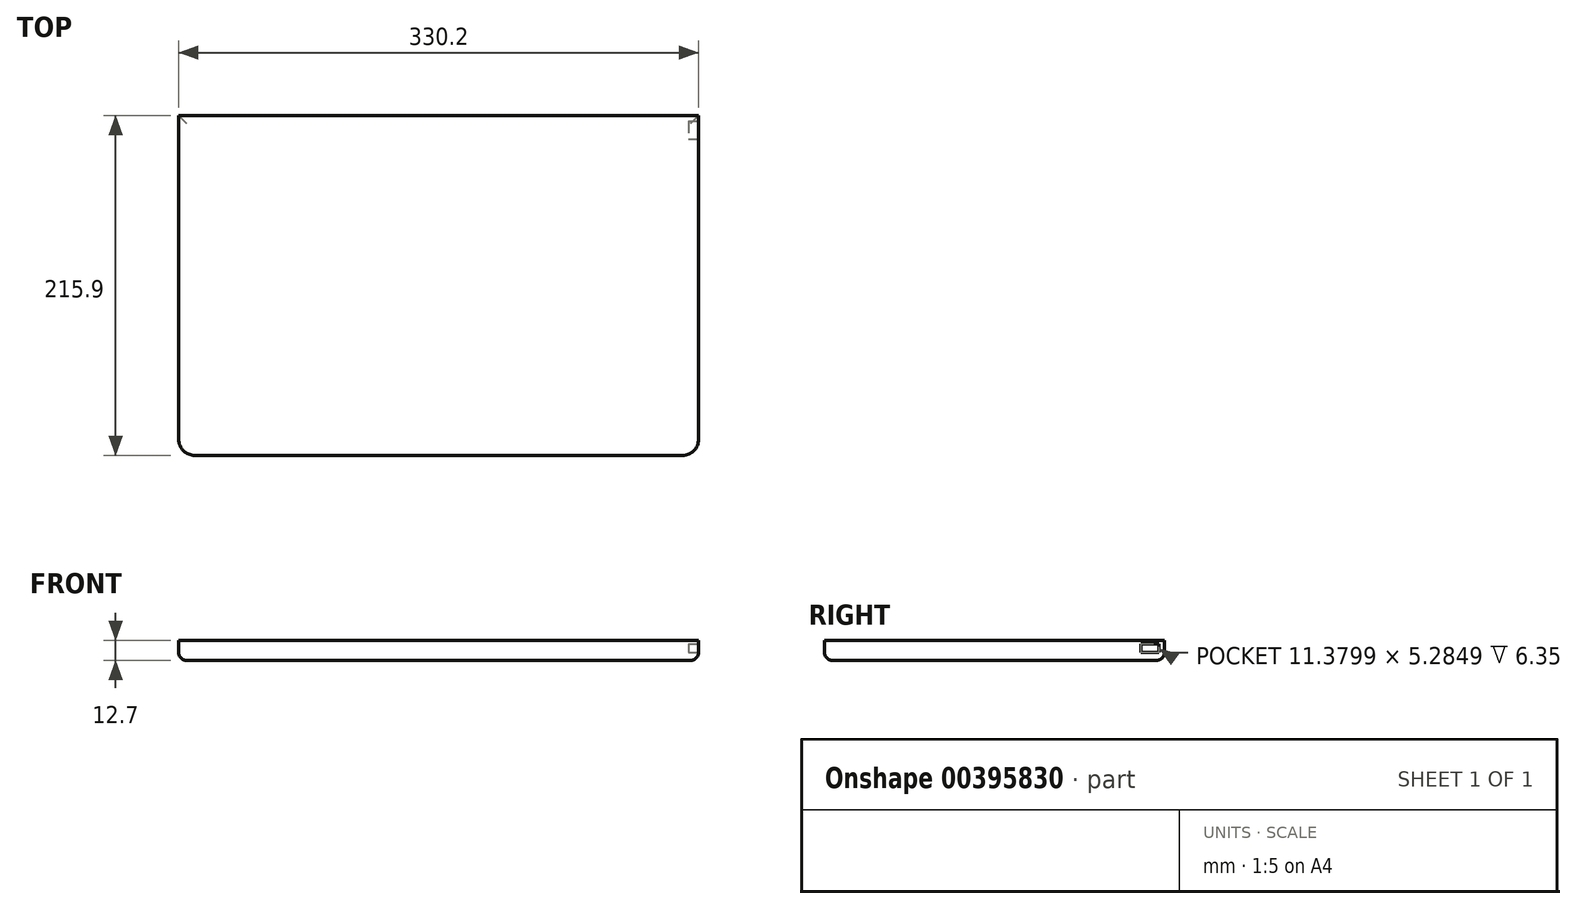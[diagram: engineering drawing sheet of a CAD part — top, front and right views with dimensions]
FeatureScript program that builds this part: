
annotation { "Feature Type Name" : "Feature", "Feature Type Description" : "" }
export const myFeature = defineFeature(function(context is Context, id is Id, definition is map)
    precondition{}
    {
        {
            var Q0;
            Q0=qCreatedBy(makeId("Top.planeOp"),FACE);
            var sketch = newSketch(context, id + "F0", { "sketchPlane" : qUnion([Q0])});
            skLineSegment(sketch, "E0.bottom", {"start": v(165.1, -107.95) * mm, "end": v(-165.1, -107.95) * mm});
            skLineSegment(sketch, "E0.top", {"start": v(165.1, 107.95) * mm, "end": v(-165.1, 107.95) * mm});
            skLineSegment(sketch, "E0.left", {"start": v(165.1, -107.95) * mm, "end": v(165.1, 107.95) * mm});
            skLineSegment(sketch, "E0.right", {"start": v(-165.1, -107.95) * mm, "end": v(-165.1, 107.95) * mm});
            skPoint(sketch, "E0.middle", {"position": v(0, 0) * mm});
            skSolve(sketch);
        }
        {
            var Q0;
            Q0=makeQuery(id+"F0.imprint","IMPRINT",FACE,{"disambiguationData":[TD([[makeQuery(id+"F0.imprint","IMPRINT",EDGE,{"derivedFrom":sQuery(id+"F0.wireOp",EDGE,"E0.bottom")}),-1.0]])]});
            extrude(context, id + "F1", {"entities" : qUnion([Q0]), "depth" : -12.7 * mm});
        }
        {
            var Q0;
            Q0=makeQuery(id+"F1.opExtrude","SWEPT_EDGE",EDGE,{"disambiguationData":[OSD([sQuery(id+"F0.wireOp",EDGE,"E0.bottom"),sQuery(id+"F0.wireOp",EDGE,"E0.left")])]});
            fillet(context, id + "F2", {"entities" : qUnion([Q0]), "radius" : 10.16 * mm, "tangentPropagation" : true, "allowEdgeOverflow" : false});
        }
        {
            var Q0;
            Q0=makeQuery(id+"F1.opExtrude","SWEPT_EDGE",EDGE,{"disambiguationData":[OSD([sQuery(id+"F0.wireOp",EDGE,"E0.bottom"),sQuery(id+"F0.wireOp",EDGE,"E0.right")])]});
            fillet(context, id + "F3", {"entities" : qUnion([Q0]), "radius" : 10.16 * mm, "tangentPropagation" : true, "allowEdgeOverflow" : false});
        }
        {
            var Q0;
            Q0=makeQuery(id+"F1.opExtrude","CAP_FACE",FACE,{"disambiguationData":[OSD([sQuery(id+"F0.wireOp",EDGE,"E0.bottom"),sQuery(id+"F0.wireOp",EDGE,"E0.top"),sQuery(id+"F0.wireOp",EDGE,"E0.left"),sQuery(id+"F0.wireOp",EDGE,"E0.right")])],"isStart":false});
            fillet(context, id + "F4", {"entities" : qUnion([Q0]), "radius" : 5.08 * mm, "tangentPropagation" : true, "allowEdgeOverflow" : false});
        }
        {
            var Q0;
            Q0=makeQuery(id+"F1.opExtrude","SWEPT_FACE",FACE,{"disambiguationData":[OSD([sQuery(id+"F0.wireOp",EDGE,"E0.left")])]});
            var sketch = newSketch(context, id + "F5", { "sketchPlane" : qUnion([Q0])});
            skLineSegment(sketch, "E1.bottom", {"start": v(105.13, -7.62) * mm, "end": v(89.9, -7.62) * mm});
            skLineSegment(sketch, "E1.top", {"start": v(105.13, -3.05) * mm, "end": v(89.9, -3.05) * mm});
            skLineSegment(sketch, "E1.left", {"start": v(105.13, -7.62) * mm, "end": v(105.13, -3.05) * mm});
            skLineSegment(sketch, "E1.right", {"start": v(89.9, -7.62) * mm, "end": v(89.9, -3.05) * mm});
            skPoint(sketch, "E1.middle", {"position": v(97.51, -5.33) * mm});
            skSolve(sketch);
        }
        {
            var Q0;
            Q0=makeQuery(id+"F5.imprint","IMPRINT",FACE,{"disambiguationData":[TD([[makeQuery(id+"F5.imprint","IMPRINT",EDGE,{"derivedFrom":sQuery(id+"F5.wireOp",EDGE,"E1.bottom")}),1.0]])]});
            extrude(context, id + "F6", {"entities" : qUnion([Q0]), "operationType" : NewBodyOperationType.ADD, "depth" : -10.16 * mm});
        }
        {
            var Q0;
            Q0=makeQuery(id+"F1.opExtrude","SWEPT_FACE",FACE,{"disambiguationData":[OSD([sQuery(id+"F0.wireOp",EDGE,"E0.left")])]});
            var sketch = newSketch(context, id + "F7", { "sketchPlane" : qUnion([Q0])});
            skLineSegment(sketch, "E2.bottom", {"start": v(104.3, -2.34) * mm, "end": v(92.93, -2.34) * mm});
            skLineSegment(sketch, "E2.top", {"start": v(104.3, -7.62) * mm, "end": v(92.93, -7.62) * mm});
            skLineSegment(sketch, "E2.left", {"start": v(104.3, -2.34) * mm, "end": v(104.3, -7.62) * mm});
            skLineSegment(sketch, "E2.right", {"start": v(92.93, -2.34) * mm, "end": v(92.93, -7.62) * mm});
            skSolve(sketch);
        }
        {
            var Q0;
            Q0=makeQuery(id+"F7.imprint","IMPRINT",FACE,{"disambiguationData":[TD([[makeQuery(id+"F7.imprint","IMPRINT",EDGE,{"derivedFrom":sQuery(id+"F7.wireOp",EDGE,"E2.bottom")}),1.0]])]});
            extrude(context, id + "F8", {"entities" : qUnion([Q0]), "operationType" : NewBodyOperationType.REMOVE, "oppositeDirection" : true, "depth" : 6.35 * mm});
        }
    });
